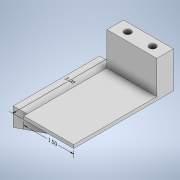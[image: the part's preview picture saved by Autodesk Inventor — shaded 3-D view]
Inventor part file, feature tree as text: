
AUTODESK INVENTOR PART (.ipt)
format: ipt  version: 2020 (Build 240168000, 168)  size: 144,896 bytes
history: native  units: in
note: dims shown in document units (in); Inventor stores cm internally (conversion verified against a paired STEP export)
features: sketch x4, other x3, extrude x3, hole x1, chamfer x1
ambient origin geometry x8: Origin, YZ Plane, XZ Plane, XY Plane, X Axis, Y Axis, Z Axis, Center Point
bodies: Solid1 (feature_tree)
feature tree (12):
  other  "Annotations"
  extrude  "Extrusion1"  Depth=3.0in
  extrude  "Extrusion2"  Depth=1.5in
  hole  "Hole1"  [1 undecoded]
  extrude  "Extrusion3"  Depth=0.5in
  chamfer  "Chamfer3"  Distance=0.4in
  sketch  "Sketch1"  dims[d0=1.5in d1=3.0in]
  sketch  "Sketch2"  dims[d2=0.1in d3=0.0in d4=1.5in]
  sketch  "Sketch6"  dims[d5=0.5in d6=1.0in d7=0.0in]
  sketch  "Sketch7"  dims[d8=0.375in d9=0.375in d10=0.2in d11=0.75in d12=0.75in d13=0.188in d14=0.5635in d15=0.5in d16=0.8108in d23=0.4in d24=0.2in d25=0.2in d26=1.62in d27=0.56in d28=0.0in d35=1.62in d36=0.56in d37=45.0deg d17=0.0in d18=0.3937in d19=1.5in d20=0.1641in d21=0.2363in d22=3.0in d29=0.5in d30=0.0344in]
  other  "Linear Dimension 1"
  other  "Linear Dimension 2"
note: 1 required parameter value undecoded (feature->parameter linkage not recoverable at this tier; creation-order binding heuristic only, values carry confidence <= 0.55)
